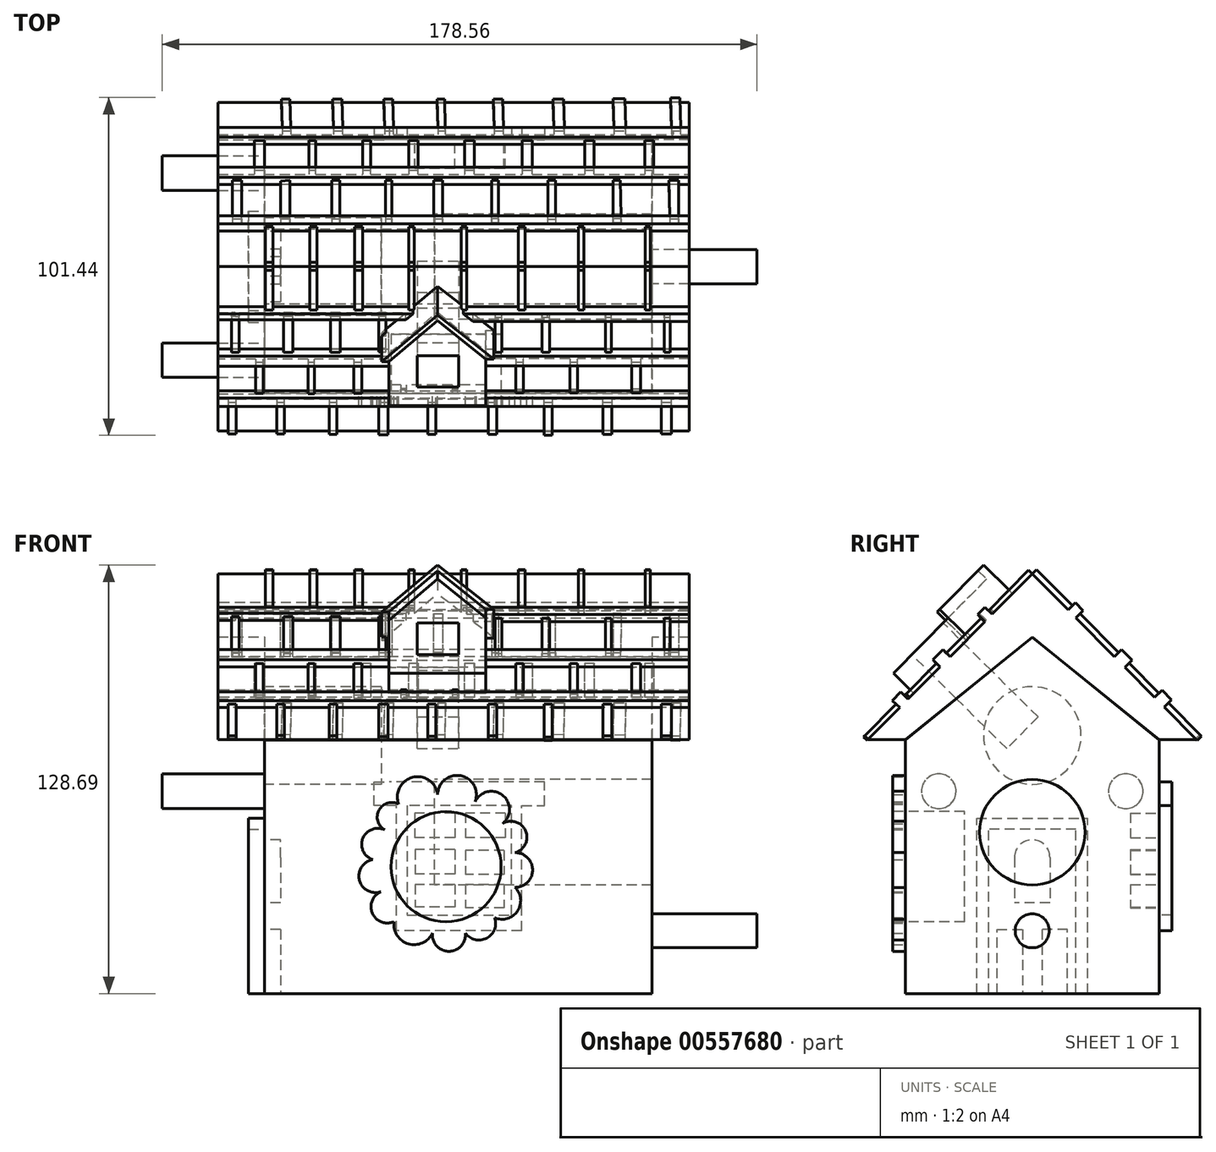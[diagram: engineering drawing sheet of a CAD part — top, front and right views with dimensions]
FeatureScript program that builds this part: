
annotation { "Feature Type Name" : "Feature", "Feature Type Description" : "" }
export const myFeature = defineFeature(function(context is Context, id is Id, definition is map)
    precondition{}
    {
        {
            var Q0;
            Q0=qCreatedBy(makeId("Right.planeOp"),FACE);
            var sketch = newSketch(context, id + "F0", { "sketchPlane" : qUnion([Q0])});
            skLineSegment(sketch, "E0.bottom", {"start": v(38.1, 38.1) * mm, "end": v(-38.1, 38.1) * mm});
            skLineSegment(sketch, "E0.top", {"start": v(38.1, -38.1) * mm, "end": v(-38.1, -38.1) * mm});
            skLineSegment(sketch, "E0.left", {"start": v(38.1, 38.1) * mm, "end": v(38.1, -38.1) * mm});
            skLineSegment(sketch, "E0.right", {"start": v(-38.1, 38.1) * mm, "end": v(-38.1, -38.1) * mm});
            skPoint(sketch, "E0.middle", {"position": v(0, 0) * mm});
            skCircle(sketch, "E1", {"center": v(0, 10.38) * mm, "radius": 15.83 * mm});
            skLineSegment(sketch, "E2", {"start": v(-38.1, 38.1) * mm, "end": v(0, 68.98) * mm});
            skLineSegment(sketch, "E3", {"start": v(0, 68.98) * mm, "end": v(38.1, 38.1) * mm});
            skSolve(sketch);
        }
        {
            var Q0;
            Q0 = qSketchRegion(id + "F0", true);
            extrude(context, id + "F1", {"entities" : qUnion([Q0]), "depth" : 14.73 * mm, "offsetDistance" : 25.4 * mm});
        }
        {
            var Q0;
            Q0=qCreatedBy(makeId("Right.planeOp"),FACE);
            var sketch = newSketch(context, id + "F2", { "sketchPlane" : qUnion([Q0])});
            skCircle(sketch, "E4", {"center": v(0, -19.24) * mm, "radius": 5.12 * mm});
            skSolve(sketch);
        }
        {
            var Q0;
            Q0 = qSketchRegion(id + "F2", true);
            extrude(context, id + "F3", {"entities" : qUnion([Q0]), "operationType" : NewBodyOperationType.ADD, "depth" : 46.23 * mm, "offsetDistance" : 25.4 * mm});
        }
        {
            var Q0;
            Q0=qCreatedBy(makeId("Right.planeOp"),FACE);
            var sketch = newSketch(context, id + "F4", { "sketchPlane" : qUnion([Q0])});
            skLineSegment(sketch, "E5", {"start": v(-38.15, 38.14) * mm, "end": v(0, 68.94) * mm});
            skLineSegment(sketch, "E6.MirrorCS", {"start": v(38.15, 38.14) * mm, "end": v(0, 68.94) * mm});
            skPoint(sketch, "E7.start.orphan", {"position": v(0, 72.65) * mm});
            skPoint(sketch, "E8.start.orphan", {"position": v(-57.02, 39.24) * mm});
            skLineSegment(sketch, "E9", {"start": v(-38.15, 38.14) * mm, "end": v(-44.95, 38.14) * mm});
            skPoint(sketch, "E10.MirrorCS.end.orphan", {"position": v(57.02, 39.24) * mm});
            skPoint(sketch, "E11.MirrorCS.end.orphan", {"position": v(38.15, 38.14) * mm});
            skLineSegment(sketch, "E12.MirrorCS", {"start": v(38.15, 38.14) * mm, "end": v(44.95, 38.14) * mm});
            skLineSegment(sketch, "E13", {"start": v(44.95, 38.14) * mm, "end": v(49.34, 38.14) * mm});
            skLineSegment(sketch, "E14", {"start": v(49.34, 38.14) * mm, "end": v(0, 87.99) * mm});
            skLineSegment(sketch, "E15.MirrorCS", {"start": v(-44.95, 38.14) * mm, "end": v(-49.34, 38.14) * mm});
            skLineSegment(sketch, "E16.MirrorCS", {"start": v(-49.34, 38.14) * mm, "end": v(0, 87.99) * mm});
            skSolve(sketch);
        }
        {
            var Q0;
            Q0 = qSketchRegion(id + "F4", true);
            extrude(context, id + "F5", {"entities" : qUnion([Q0]), "operationType" : NewBodyOperationType.ADD, "depth" : 25.9 * mm, "offsetDistance" : 25.4 * mm});
        }
        {
            var Q0;
            Q0=makeQuery(id+"F5.boolean.opBoolean","MERGE",FACE,{"derivedFrom":[makeQuery(id+"F1.opExtrude","CAP_FACE",FACE,{"disambiguationData":[OSD([sQuery(id+"F0.wireOp",EDGE,"E0.top"),sQuery(id+"F0.wireOp",EDGE,"E0.left"),sQuery(id+"F0.wireOp",EDGE,"E0.right"),sQuery(id+"F0.wireOp",EDGE,"E1"),sQuery(id+"F0.wireOp",EDGE,"E2"),sQuery(id+"F0.wireOp",EDGE,"E3")])],"isStart":true}),makeQuery(id+"F5.opExtrude","CAP_FACE",FACE,{"disambiguationData":[OSD([sQuery(id+"F4.wireOp",EDGE,"E5"),sQuery(id+"F4.wireOp",EDGE,"E6.MirrorCS"),sQuery(id+"F4.wireOp",EDGE,"E9"),sQuery(id+"F4.wireOp",EDGE,"mGPt1msT-ov7u-mBRv-SWqM-muiSPzfu6SFx"),sQuery(id+"F4.wireOp",EDGE,"db452817-d711-4797-9ae9-b6f5df7f732d0.MirrorCS"),sQuery(id+"F4.wireOp",EDGE,"E12.MirrorCS")])],"isStart":true})]});
            extrude(context, id + "F6", {"entities" : qUnion([Q0]), "operationType" : NewBodyOperationType.ADD, "depth" : 101.6 * mm, "offsetDistance" : 25.4 * mm});
        }
        {
            var Q0;
            Q0=makeQuery(id+"F6.opExtrude","CAP_FACE",FACE,{"disambiguationData":[OSD([sQuery(id+"F0.wireOp",EDGE,"E0.top"),sQuery(id+"F0.wireOp",EDGE,"E0.left"),sQuery(id+"F0.wireOp",EDGE,"E0.right"),sQuery(id+"F0.wireOp",EDGE,"E1"),sQuery(id+"F0.wireOp",EDGE,"E2"),sQuery(id+"F0.wireOp",EDGE,"E3"),sQuery(id+"F4.wireOp",EDGE,"E5"),sQuery(id+"F4.wireOp",EDGE,"E6.MirrorCS"),sQuery(id+"F4.wireOp",EDGE,"E9"),sQuery(id+"F4.wireOp",EDGE,"mGPt1msT-ov7u-mBRv-SWqM-muiSPzfu6SFx"),sQuery(id+"F4.wireOp",EDGE,"db452817-d711-4797-9ae9-b6f5df7f732d0.MirrorCS"),sQuery(id+"F4.wireOp",EDGE,"E12.MirrorCS")])],"isStart":false});
            var sketch = newSketch(context, id + "F7", { "sketchPlane" : qUnion([Q0])});
            skCircle(sketch, "E17", {"center": v(0, 10.38) * mm, "radius": 15.83 * mm});
            skPoint(sketch, "E17.first.point", {"position": v(-11.76, 20.98) * mm});
            skPoint(sketch, "E17.second.point", {"position": v(11.95, 0) * mm});
            skPoint(sketch, "E17.third.point", {"position": v(14.73, 16.19) * mm});
            skSolve(sketch);
        }
        {
            var Q0;
            Q0 = qSketchRegion(id + "F7", true);
            extrude(context, id + "F8", {"entities" : qUnion([Q0]), "operationType" : NewBodyOperationType.ADD, "oppositeDirection" : true, "depth" : 51.05 * mm, "offsetDistance" : 25.4 * mm});
        }
        {
            var Q0;
            Q0=makeQuery(id+"F8.boolean.opBoolean","MERGE",FACE,{"derivedFrom":[makeQuery(id+"F6.opExtrude","CAP_FACE",FACE,{"disambiguationData":[OSD([sQuery(id+"F0.wireOp",EDGE,"E0.top"),sQuery(id+"F0.wireOp",EDGE,"E0.left"),sQuery(id+"F0.wireOp",EDGE,"E0.right"),sQuery(id+"F0.wireOp",EDGE,"E1"),sQuery(id+"F0.wireOp",EDGE,"E2"),sQuery(id+"F0.wireOp",EDGE,"E3"),sQuery(id+"F4.wireOp",EDGE,"E5"),sQuery(id+"F4.wireOp",EDGE,"E6.MirrorCS"),sQuery(id+"F4.wireOp",EDGE,"E9"),sQuery(id+"F4.wireOp",EDGE,"mGPt1msT-ov7u-mBRv-SWqM-muiSPzfu6SFx"),sQuery(id+"F4.wireOp",EDGE,"db452817-d711-4797-9ae9-b6f5df7f732d0.MirrorCS"),sQuery(id+"F4.wireOp",EDGE,"E12.MirrorCS")])],"isStart":false}),makeQuery(id+"F8.opExtrude","CAP_FACE",FACE,{"disambiguationData":[OSD([sQuery(id+"F7.wireOp",EDGE,"E17")])],"isStart":true})]});
            var sketch = newSketch(context, id + "F9", { "sketchPlane" : qUnion([Q0])});
            skLineSegment(sketch, "E18", {"start": v(-16.68, -38.1) * mm, "end": v(-16.68, 14.56) * mm});
            skLineSegment(sketch, "E19", {"start": v(-16.68, 14.56) * mm, "end": v(-2.36, 14.56) * mm});
            skLineSegment(sketch, "E20", {"start": v(-13.13, -38.1) * mm, "end": v(-16.68, -38.1) * mm});
            skLineSegment(sketch, "E21.MirrorCS", {"start": v(16.68, 14.56) * mm, "end": v(2.36, 14.56) * mm});
            skLineSegment(sketch, "E22.MirrorCS", {"start": v(16.68, -38.1) * mm, "end": v(16.68, 14.56) * mm});
            skLineSegment(sketch, "E23.MirrorCS", {"start": v(13.13, -38.1) * mm, "end": v(16.68, -38.1) * mm});
            skLineSegment(sketch, "E24", {"start": v(-2.36, 14.56) * mm, "end": v(2.36, 14.56) * mm});
            skLineSegment(sketch, "E25", {"start": v(-13.13, -38.1) * mm, "end": v(-13.13, 11.21) * mm});
            skLineSegment(sketch, "E26", {"start": v(-13.13, 11.21) * mm, "end": v(0, 11.21) * mm});
            skLineSegment(sketch, "E27.MirrorCS", {"start": v(13.13, 11.21) * mm, "end": v(0, 11.21) * mm});
            skLineSegment(sketch, "E28.MirrorCS", {"start": v(13.13, -38.1) * mm, "end": v(13.13, 11.21) * mm});
            skPoint(sketch, "E29.start.orphan", {"position": v(-2.36, -38.1) * mm});
            skPoint(sketch, "E30.orphan", {"position": v(2.36, -38.1) * mm});
            skSolve(sketch);
        }
        {
            var Q0;
            Q0 = qSketchRegion(id + "F9", true);
            extrude(context, id + "F10", {"entities" : qUnion([Q0]), "operationType" : NewBodyOperationType.ADD, "depth" : 4.83 * mm, "offsetDistance" : 25.4 * mm});
        }
        {
            var Q0;
            {var subQ0=sQuery(id+"F0.wireOp",EDGE,"E0.top");Q0=makeQuery(id+"F10.boolean.opBoolean","SPLIT",FACE,{"disambiguationData":[TD([makeQuery(id+"F10.opExtrude","SWEPT_FACE",FACE,{"disambiguationData":[OSD([sQuery(id+"F9.wireOp",EDGE,"E25")])]})])],"derivedFrom":makeQuery(id+"F8.boolean.opBoolean","MERGE",FACE,{"derivedFrom":[makeQuery(id+"F6.opExtrude","CAP_FACE",FACE,{"disambiguationData":[OSD([subQ0,sQuery(id+"F0.wireOp",EDGE,"E0.left"),sQuery(id+"F0.wireOp",EDGE,"E0.right"),sQuery(id+"F0.wireOp",EDGE,"E1"),sQuery(id+"F0.wireOp",EDGE,"E2"),sQuery(id+"F0.wireOp",EDGE,"E3"),sQuery(id+"F4.wireOp",EDGE,"E5"),sQuery(id+"F4.wireOp",EDGE,"E6.MirrorCS"),sQuery(id+"F4.wireOp",EDGE,"E9"),sQuery(id+"F4.wireOp",EDGE,"mGPt1msT-ov7u-mBRv-SWqM-muiSPzfu6SFx"),sQuery(id+"F4.wireOp",EDGE,"db452817-d711-4797-9ae9-b6f5df7f732d0.MirrorCS"),sQuery(id+"F4.wireOp",EDGE,"E12.MirrorCS")])],"isStart":false}),makeQuery(id+"F8.opExtrude","CAP_FACE",FACE,{"disambiguationData":[OSD([sQuery(id+"F7.wireOp",EDGE,"E17")])],"isStart":true})]})});}
            var sketch = newSketch(context, id + "F11", { "sketchPlane" : qUnion([Q0])});
            skLineSegment(sketch, "E31", {"start": v(-5.3, 2.78) * mm, "end": v(-5.3, -10.8) * mm});
            skLineSegment(sketch, "E32.MirrorCS", {"start": v(5.3, 2.78) * mm, "end": v(5.3, -10.8) * mm});
            skArc(sketch, "E33", {"start": v(5.3, 2.78) * mm, "mid": v(0, 8.08) * mm, "end": v(-5.3, 2.78) * mm});
            skLineSegment(sketch, "E34", {"start": v(-5.3, -10.8) * mm, "end": v(5.3, -10.8) * mm});
            skLineSegment(sketch, "E35", {"start": v(-11.37, -12.68) * mm, "end": v(-11.37, -15.43) * mm});
            skLineSegment(sketch, "E36", {"start": v(-11.37, -15.43) * mm, "end": v(10.6, -15.43) * mm});
            skLineSegment(sketch, "E37", {"start": v(10.6, -15.43) * mm, "end": v(10.6, -12.52) * mm});
            skLineSegment(sketch, "E38", {"start": v(10.6, -12.52) * mm, "end": v(-11.37, -12.52) * mm});
            skLineSegment(sketch, "E39", {"start": v(-10.6, -38.1) * mm, "end": v(-10.6, -18.85) * mm});
            skLineSegment(sketch, "E40", {"start": v(-10.6, -18.85) * mm, "end": v(-2.9, -18.85) * mm});
            skLineSegment(sketch, "E41", {"start": v(-2.9, -18.85) * mm, "end": v(-2.9, -38.1) * mm});
            skLineSegment(sketch, "E42", {"start": v(-2.9, -38.1) * mm, "end": v(-10.6, -38.1) * mm});
            skLineSegment(sketch, "E43.MirrorCS", {"start": v(2.9, -18.85) * mm, "end": v(2.9, -38.1) * mm});
            skLineSegment(sketch, "E44.MirrorCS", {"start": v(10.6, -38.1) * mm, "end": v(10.6, -18.85) * mm});
            skLineSegment(sketch, "E45.MirrorCS", {"start": v(10.6, -18.85) * mm, "end": v(2.9, -18.85) * mm});
            skLineSegment(sketch, "E46.MirrorCS", {"start": v(2.9, -38.1) * mm, "end": v(10.6, -38.1) * mm});
            skSolve(sketch);
        }
        {
            var Q0;
            Q0 = qSketchRegion(id + "F11", true);
            extrude(context, id + "F12", {"entities" : qUnion([Q0]), "operationType" : NewBodyOperationType.REMOVE, "oppositeDirection" : true, "depth" : 4.83 * mm, "offsetDistance" : 25.4 * mm});
        }
        {
            var Q0;
            {var subQ0=sQuery(id+"F4.wireOp",EDGE,"E6.MirrorCS");var subQ1=sQuery(id+"F4.wireOp",EDGE,"E5");var subQ2=sQuery(id+"F4.wireOp",EDGE,"E12.MirrorCS");var subQ3=sQuery(id+"F4.wireOp",EDGE,"E9");var subQ4=sQuery(id+"F0.wireOp",EDGE,"E2");var subQ5=sQuery(id+"F4.wireOp",EDGE,"db452817-d711-4797-9ae9-b6f5df7f732d0.MirrorCS");var subQ6=sQuery(id+"F0.wireOp",EDGE,"E0.right");var subQ7=sQuery(id+"F4.wireOp",EDGE,"mGPt1msT-ov7u-mBRv-SWqM-muiSPzfu6SFx");var subQ8=sQuery(id+"F0.wireOp",EDGE,"E0.left");var subQ9=sQuery(id+"F0.wireOp",EDGE,"E3");var subQ10=sQuery(id+"F0.wireOp",EDGE,"E0.top");Q0=makeQuery(id+"F10.boolean.opBoolean","SPLIT",FACE,{"disambiguationData":[TD([makeQuery(id+"F1.opExtrude","SWEPT_FACE",FACE,{"disambiguationData":[OSD([subQ8])]})])],"derivedFrom":makeQuery(id+"F8.boolean.opBoolean","MERGE",FACE,{"derivedFrom":[makeQuery(id+"F6.opExtrude","CAP_FACE",FACE,{"disambiguationData":[OSD([subQ10,subQ8,subQ6,sQuery(id+"F0.wireOp",EDGE,"E1"),subQ4,subQ9,subQ1,subQ0,subQ3,subQ7,subQ5,subQ2])],"isStart":false}),makeQuery(id+"F8.opExtrude","CAP_FACE",FACE,{"disambiguationData":[OSD([sQuery(id+"F7.wireOp",EDGE,"E17")])],"isStart":true})]})});}
            var sketch = newSketch(context, id + "F13", { "sketchPlane" : qUnion([Q0])});
            skCircle(sketch, "E47", {"center": v(0, 39.42) * mm, "radius": 14.66 * mm});
            skSolve(sketch);
        }
        {
            var Q0;
            Q0 = qSketchRegion(id + "F13", true);
            extrude(context, id + "F14", {"entities" : qUnion([Q0]), "operationType" : NewBodyOperationType.REMOVE, "oppositeDirection" : true, "depth" : 35.05 * mm, "offsetDistance" : 25.4 * mm});
        }
        {
            var Q0;
            {var subQ0=sQuery(id+"F4.wireOp",EDGE,"E6.MirrorCS");var subQ1=sQuery(id+"F4.wireOp",EDGE,"E5");var subQ2=sQuery(id+"F4.wireOp",EDGE,"E12.MirrorCS");var subQ3=sQuery(id+"F4.wireOp",EDGE,"E9");var subQ4=sQuery(id+"F0.wireOp",EDGE,"E2");var subQ5=sQuery(id+"F4.wireOp",EDGE,"db452817-d711-4797-9ae9-b6f5df7f732d0.MirrorCS");var subQ6=sQuery(id+"F0.wireOp",EDGE,"E0.right");var subQ7=sQuery(id+"F4.wireOp",EDGE,"mGPt1msT-ov7u-mBRv-SWqM-muiSPzfu6SFx");var subQ8=sQuery(id+"F0.wireOp",EDGE,"E0.left");var subQ9=sQuery(id+"F0.wireOp",EDGE,"E3");var subQ10=sQuery(id+"F0.wireOp",EDGE,"E0.top");Q0=makeQuery(id+"F10.boolean.opBoolean","SPLIT",FACE,{"disambiguationData":[TD([makeQuery(id+"F1.opExtrude","SWEPT_FACE",FACE,{"disambiguationData":[OSD([subQ8])]})])],"derivedFrom":makeQuery(id+"F8.boolean.opBoolean","MERGE",FACE,{"derivedFrom":[makeQuery(id+"F6.opExtrude","CAP_FACE",FACE,{"disambiguationData":[OSD([subQ10,subQ8,subQ6,sQuery(id+"F0.wireOp",EDGE,"E1"),subQ4,subQ9,subQ1,subQ0,subQ3,subQ7,subQ5,subQ2])],"isStart":false}),makeQuery(id+"F8.opExtrude","CAP_FACE",FACE,{"disambiguationData":[OSD([sQuery(id+"F7.wireOp",EDGE,"E17")])],"isStart":true})]})});}
            var sketch = newSketch(context, id + "F15", { "sketchPlane" : qUnion([Q0])});
            skCircle(sketch, "E48", {"center": v(-28.08, 22.67) * mm, "radius": 5.2 * mm});
            skCircle(sketch, "E49.MirrorC", {"center": v(28.08, 22.67) * mm, "radius": 5.2 * mm});
            skSolve(sketch);
        }
        {
            var Q0;
            Q0 = qSketchRegion(id + "F15", true);
            extrude(context, id + "F16", {"entities" : qUnion([Q0]), "operationType" : NewBodyOperationType.ADD, "depth" : 30.73 * mm, "offsetDistance" : 25.4 * mm});
        }
        {
            var Q0;
            {var subQ0=sQuery(id+"F4.wireOp",EDGE,"E6.MirrorCS");var subQ1=sQuery(id+"F4.wireOp",EDGE,"E5");var subQ2=sQuery(id+"F4.wireOp",EDGE,"E16.MirrorCS");var subQ3=sQuery(id+"F4.wireOp",EDGE,"E15.MirrorCS");var subQ4=sQuery(id+"F4.wireOp",EDGE,"E9");var subQ5=sQuery(id+"F0.wireOp",EDGE,"E2");var subQ6=sQuery(id+"F4.wireOp",EDGE,"E14");var subQ7=sQuery(id+"F0.wireOp",EDGE,"E0.right");var subQ8=sQuery(id+"F4.wireOp",EDGE,"E13");var subQ9=sQuery(id+"F4.wireOp",EDGE,"E12.MirrorCS");var subQ10=sQuery(id+"F0.wireOp",EDGE,"E0.left");var subQ11=sQuery(id+"F0.wireOp",EDGE,"E3");var subQ12=sQuery(id+"F0.wireOp",EDGE,"E0.top");Q0=makeQuery(id+"F10.boolean.opBoolean","SPLIT",FACE,{"disambiguationData":[TD([makeQuery(id+"F1.opExtrude","SWEPT_FACE",FACE,{"disambiguationData":[OSD([subQ10])]})])],"derivedFrom":makeQuery(id+"F8.boolean.opBoolean","MERGE",FACE,{"derivedFrom":[makeQuery(id+"F6.opExtrude","CAP_FACE",FACE,{"disambiguationData":[OSD([subQ12,subQ10,subQ7,sQuery(id+"F0.wireOp",EDGE,"E1"),subQ5,subQ11,subQ1,subQ0,subQ4,subQ9,subQ8,subQ6,subQ3,subQ2])],"isStart":false}),makeQuery(id+"F8.opExtrude","CAP_FACE",FACE,{"disambiguationData":[OSD([sQuery(id+"F7.wireOp",EDGE,"E17")])],"isStart":true})]})});}
            var sketch = newSketch(context, id + "F17", { "sketchPlane" : qUnion([Q0])});
            skLineSegment(sketch, "E50", {"start": v(-49.34, 38.14) * mm, "end": v(0, 87.99) * mm});
            skLineSegment(sketch, "E51", {"start": v(0, 87.99) * mm, "end": v(49.34, 38.14) * mm});
            skLineSegment(sketch, "E52", {"start": v(49.34, 38.14) * mm, "end": v(38.15, 38.14) * mm});
            skLineSegment(sketch, "E53", {"start": v(-49.34, 38.14) * mm, "end": v(-38.15, 38.14) * mm});
            skLineSegment(sketch, "E54", {"start": v(-38.15, 38.14) * mm, "end": v(0, 69.05) * mm});
            skLineSegment(sketch, "E55", {"start": v(0, 69.05) * mm, "end": v(38.15, 38.14) * mm});
            skSolve(sketch);
        }
        {
            var Q0;
            Q0 = qSketchRegion(id + "F17", true);
            extrude(context, id + "F18", {"entities" : qUnion([Q0]), "operationType" : NewBodyOperationType.ADD, "depth" : 13.97 * mm, "offsetDistance" : 25.4 * mm});
        }
        {
            var Q0;
            {var subQ0=sQuery(id+"F4.wireOp",EDGE,"E16.MirrorCS");Q0=makeQuery(id+"F18.boolean.opBoolean","MERGE",FACE,{"derivedFrom":[makeQuery(id+"F6.boolean.opBoolean","MERGE",FACE,{"derivedFrom":[makeQuery(id+"F5.opExtrude","SWEPT_FACE",FACE,{"disambiguationData":[OSD([subQ0])]}),makeQuery(id+"F6.opExtrude","SWEPT_FACE",FACE,{"disambiguationData":[OSD([subQ0])]})]}),makeQuery(id+"F18.opExtrude","SWEPT_FACE",FACE,{"disambiguationData":[OSD([sQuery(id+"F17.wireOp",EDGE,"E51")])]})]});}
            var sketch = newSketch(context, id + "F19", { "sketchPlane" : qUnion([Q0])});
            skLineSegment(sketch, "E56", {"start": v(-64.2, 11.96) * mm, "end": v(-64.2, 34.31) * mm});
            skLineSegment(sketch, "E57", {"start": v(-64.2, 34.31) * mm, "end": v(-49.73, 51.77) * mm});
            skLineSegment(sketch, "E58", {"start": v(-49.73, 51.77) * mm, "end": v(-35.25, 35.38) * mm});
            skLineSegment(sketch, "E59", {"start": v(-35.25, 35.38) * mm, "end": v(-35.25, 11.96) * mm});
            skLineSegment(sketch, "E60", {"start": v(-35.25, 11.96) * mm, "end": v(-64.2, 11.96) * mm});
            skSolve(sketch);
        }
        {
            var Q0;
            Q0=makeQuery(id+"F19.imprint","IMPRINT",FACE,{"disambiguationData":[TD([[makeQuery(id+"F19.imprint","IMPRINT",EDGE,{"derivedFrom":sQuery(id+"F19.wireOp",EDGE,"E56")}),-1.0]])]});
            extrude(context, id + "F20", {"entities" : qUnion([Q0]), "operationType" : NewBodyOperationType.ADD, "depth" : 8.64 * mm, "offsetDistance" : 25.4 * mm});
        }
        {
            var Q0;
            {var subQ0=sQuery(id+"F4.wireOp",EDGE,"E16.MirrorCS");Q0=makeQuery(id+"F18.boolean.opBoolean","MERGE",FACE,{"derivedFrom":[makeQuery(id+"F6.boolean.opBoolean","MERGE",FACE,{"derivedFrom":[makeQuery(id+"F5.opExtrude","SWEPT_FACE",FACE,{"disambiguationData":[OSD([subQ0])]}),makeQuery(id+"F6.opExtrude","SWEPT_FACE",FACE,{"disambiguationData":[OSD([subQ0])]})]}),makeQuery(id+"F18.opExtrude","SWEPT_FACE",FACE,{"disambiguationData":[OSD([sQuery(id+"F17.wireOp",EDGE,"E51")])]})]});}
            var sketch = newSketch(context, id + "F21", { "sketchPlane" : qUnion([Q0])});
            skLineSegment(sketch, "E61", {"start": v(-35.25, 35.38) * mm, "end": v(-32.72, 35.38) * mm});
            skLineSegment(sketch, "E62", {"start": v(-32.72, 35.38) * mm, "end": v(-49.73, 54.13) * mm});
            skLineSegment(sketch, "E63", {"start": v(-64.2, 34.31) * mm, "end": v(-66.44, 34.31) * mm});
            skLineSegment(sketch, "E64", {"start": v(-66.44, 34.31) * mm, "end": v(-49.73, 54.13) * mm});
            skLineSegment(sketch, "E65", {"start": v(-64.2, 34.31) * mm, "end": v(-49.73, 51.77) * mm});
            skLineSegment(sketch, "E66", {"start": v(-49.73, 51.77) * mm, "end": v(-35.25, 35.38) * mm});
            skSolve(sketch);
        }
        {
            var Q0;
            Q0 = qSketchRegion(id + "F21", true);
            extrude(context, id + "F22", {"entities" : qUnion([Q0]), "operationType" : NewBodyOperationType.ADD, "depth" : 12.2 * mm, "offsetDistance" : 25.4 * mm});
        }
        {
            var Q0;
            Q0=makeQuery(id+"F20.opExtrude","CAP_FACE",FACE,{"disambiguationData":[OSD([sQuery(id+"F19.wireOp",EDGE,"E56"),sQuery(id+"F19.wireOp",EDGE,"E57"),sQuery(id+"F19.wireOp",EDGE,"E58"),sQuery(id+"F19.wireOp",EDGE,"E59"),sQuery(id+"F19.wireOp",EDGE,"E60")])],"isStart":false});
            var sketch = newSketch(context, id + "F23", { "sketchPlane" : qUnion([Q0])});
            skLineSegment(sketch, "E67.bottom", {"start": v(-55.74, 33.2) * mm, "end": v(-43.38, 33.2) * mm});
            skLineSegment(sketch, "E67.top", {"start": v(-55.74, 19.83) * mm, "end": v(-43.38, 19.83) * mm});
            skLineSegment(sketch, "E67.left", {"start": v(-55.74, 33.2) * mm, "end": v(-55.74, 19.83) * mm});
            skLineSegment(sketch, "E67.right", {"start": v(-43.38, 33.2) * mm, "end": v(-43.38, 19.83) * mm});
            skSolve(sketch);
        }
        {
            var Q0;
            Q0 = qSketchRegion(id + "F23", true);
            extrude(context, id + "F24", {"entities" : qUnion([Q0]), "operationType" : NewBodyOperationType.REMOVE, "oppositeDirection" : true, "depth" : 40.13 * mm, "offsetDistance" : 25.4 * mm});
        }
        {
            var Q0;
            {var subQ0=sQuery(id+"F0.wireOp",EDGE,"E0.right");Q0=makeQuery(id+"F6.boolean.opBoolean","MERGE",FACE,{"derivedFrom":[makeQuery(id+"F1.opExtrude","SWEPT_FACE",FACE,{"disambiguationData":[OSD([subQ0])]}),makeQuery(id+"F6.opExtrude","SWEPT_FACE",FACE,{"disambiguationData":[OSD([subQ0])]})]});}
            var sketch = newSketch(context, id + "F25", { "sketchPlane" : qUnion([Q0])});
            skArc(sketch, "E68", {"start": v(-49.62, 21.7) * mm, "mid": v(-57.13, 26.86) * mm, "end": v(-61.3, 18.76) * mm});
            skArc(sketch, "E69", {"start": v(-38.55, 19.18) * mm, "mid": v(-42.53, 27.3) * mm, "end": v(-49.62, 21.7) * mm});
            skArc(sketch, "E70", {"start": v(-30.16, 12.93) * mm, "mid": v(-30.25, 21.56) * mm, "end": v(-38.55, 19.18) * mm});
            skArc(sketch, "E71", {"start": v(-26.4, 4.22) * mm, "mid": v(-23.22, 10.76) * mm, "end": v(-30.16, 12.93) * mm});
            skArc(sketch, "E72", {"start": v(-26.4, -6.21) * mm, "mid": v(-21.13, -1) * mm, "end": v(-26.4, 4.22) * mm});
            skArc(sketch, "E73", {"start": v(-32.5, -15.3) * mm, "mid": v(-25.65, -13.32) * mm, "end": v(-26.4, -6.21) * mm});
            skArc(sketch, "E74", {"start": v(-41.34, -19.93) * mm, "mid": v(-34.92, -21.46) * mm, "end": v(-32.5, -15.3) * mm});
            skArc(sketch, "E75", {"start": v(-51.17, -19.93) * mm, "mid": v(-46.26, -25.43) * mm, "end": v(-41.34, -19.93) * mm});
            skArc(sketch, "E76", {"start": v(-62.73, -16.5) * mm, "mid": v(-58.42, -23.17) * mm, "end": v(-51.17, -19.93) * mm});
            skArc(sketch, "E77", {"start": v(-66.63, -7.5) * mm, "mid": v(-69.24, -13.98) * mm, "end": v(-62.73, -16.5) * mm});
            skArc(sketch, "E78", {"start": v(-69.09, 2.12) * mm, "mid": v(-73.1, -4.03) * mm, "end": v(-66.63, -7.5) * mm});
            skArc(sketch, "E79", {"start": v(-65.2, 10.88) * mm, "mid": v(-72.02, 8.67) * mm, "end": v(-69.09, 2.12) * mm});
            skArc(sketch, "E80", {"start": v(-61.3, 18.76) * mm, "mid": v(-67.32, 16.84) * mm, "end": v(-65.2, 10.88) * mm});
            skSolve(sketch);
        }
        {
            var Q0;
            Q0 = qSketchRegion(id + "F25", true);
            extrude(context, id + "F26", {"entities" : qUnion([Q0]), "operationType" : NewBodyOperationType.ADD, "depth" : 3.8 * mm, "offsetDistance" : 25.4 * mm});
        }
        {
            var Q0;
            Q0=makeQuery(id+"F26.opExtrude","CAP_FACE",FACE,{"disambiguationData":[OSD([sQuery(id+"F25.wireOp",EDGE,"E68"),sQuery(id+"F25.wireOp",EDGE,"E69"),sQuery(id+"F25.wireOp",EDGE,"E70"),sQuery(id+"F25.wireOp",EDGE,"E71"),sQuery(id+"F25.wireOp",EDGE,"E72"),sQuery(id+"F25.wireOp",EDGE,"E73"),sQuery(id+"F25.wireOp",EDGE,"E74"),sQuery(id+"F25.wireOp",EDGE,"E75"),sQuery(id+"F25.wireOp",EDGE,"E76"),sQuery(id+"F25.wireOp",EDGE,"E77"),sQuery(id+"F25.wireOp",EDGE,"E78"),sQuery(id+"F25.wireOp",EDGE,"E79"),sQuery(id+"F25.wireOp",EDGE,"E80")])],"isStart":false});
            var sketch = newSketch(context, id + "F27", { "sketchPlane" : qUnion([Q0])});
            skCircle(sketch, "E81", {"center": v(-47.11, 0) * mm, "radius": 16.53 * mm});
            skSolve(sketch);
        }
        {
            var Q0;
            Q0 = qSketchRegion(id + "F27", true);
            extrude(context, id + "F28", {"entities" : qUnion([Q0]), "operationType" : NewBodyOperationType.REMOVE, "oppositeDirection" : true, "depth" : 21.59 * mm, "offsetDistance" : 25.4 * mm});
        }
        {
            var Q0;
            {var subQ0=sQuery(id+"F0.wireOp",EDGE,"E0.left");Q0=makeQuery(id+"F6.boolean.opBoolean","MERGE",FACE,{"derivedFrom":[makeQuery(id+"F1.opExtrude","SWEPT_FACE",FACE,{"disambiguationData":[OSD([subQ0])]}),makeQuery(id+"F6.opExtrude","SWEPT_FACE",FACE,{"disambiguationData":[OSD([subQ0])]})]});}
            var sketch = newSketch(context, id + "F29", { "sketchPlane" : qUnion([Q0])});
            skLineSegment(sketch, "E82", {"start": v(24.4, -19.25) * mm, "end": v(24.4, 18.4) * mm});
            skLineSegment(sketch, "E83", {"start": v(24.4, 18.4) * mm, "end": v(17.55, 18.4) * mm});
            skLineSegment(sketch, "E84", {"start": v(17.55, 18.4) * mm, "end": v(17.55, 25.45) * mm});
            skLineSegment(sketch, "E85", {"start": v(17.55, 25.45) * mm, "end": v(64.18, 25.45) * mm});
            skLineSegment(sketch, "E86", {"start": v(24.4, -19.25) * mm, "end": v(62.04, -19.25) * mm});
            skLineSegment(sketch, "E87", {"start": v(62.04, -19.25) * mm, "end": v(62.04, 16.9) * mm});
            skPoint(sketch, "E88.startSnap0", {"position": v(20.98, 18.4) * mm});
            skLineSegment(sketch, "E89", {"start": v(58.85, 18.4) * mm, "end": v(58.85, -14.51) * mm});
            skLineSegment(sketch, "E90", {"start": v(58.85, -14.51) * mm, "end": v(27.43, -14.51) * mm});
            skPoint(sketch, "E88.start.orphan", {"position": v(26.74, 18.4) * mm});
            skPoint(sketch, "E91.end.orphan", {"position": v(67.82, 25.24) * mm});
            skPoint(sketch, "E92.end.orphan", {"position": v(67.82, 25.45) * mm});
            skLineSegment(sketch, "E93", {"start": v(27.43, -14.51) * mm, "end": v(27.43, 16.38) * mm});
            skLineSegment(sketch, "E94", {"start": v(27.43, 16.38) * mm, "end": v(27.43, 18.4) * mm});
            skLineSegment(sketch, "E95", {"start": v(27.43, 18.4) * mm, "end": v(58.85, 18.4) * mm});
            skLineSegment(sketch, "E96", {"start": v(62.04, 16.9) * mm, "end": v(62.04, 18.4) * mm});
            skLineSegment(sketch, "E97", {"start": v(62.04, 18.4) * mm, "end": v(68.65, 18.4) * mm});
            skLineSegment(sketch, "E98", {"start": v(68.65, 18.4) * mm, "end": v(68.65, 25.5) * mm});
            skLineSegment(sketch, "E99", {"start": v(68.65, 25.5) * mm, "end": v(64.18, 25.45) * mm});
            skSolve(sketch);
        }
        {
            var Q0;
            Q0=makeQuery(id+"F29.imprint","IMPRINT",FACE,{"disambiguationData":[TD([[makeQuery(id+"F29.imprint","IMPRINT",EDGE,{"derivedFrom":sQuery(id+"F29.wireOp",EDGE,"E82")}),-1.0]])]});
            extrude(context, id + "F30", {"entities" : qUnion([Q0]), "operationType" : NewBodyOperationType.ADD, "depth" : 3.8 * mm, "offsetDistance" : 25.4 * mm});
        }
        {
            var Q0;
            {var subQ0=sQuery(id+"F0.wireOp",EDGE,"E0.left");Q0=makeQuery(id+"F30.boolean.opBoolean","SPLIT",FACE,{"disambiguationData":[TD([makeQuery(id+"F30.opExtrude","SWEPT_FACE",FACE,{"disambiguationData":[OSD([sQuery(id+"F29.wireOp",EDGE,"E89")])]})])],"derivedFrom":makeQuery(id+"F6.boolean.opBoolean","MERGE",FACE,{"derivedFrom":[makeQuery(id+"F1.opExtrude","SWEPT_FACE",FACE,{"disambiguationData":[OSD([subQ0])]}),makeQuery(id+"F6.opExtrude","SWEPT_FACE",FACE,{"disambiguationData":[OSD([subQ0])]})]})});}
            var sketch = newSketch(context, id + "F31", { "sketchPlane" : qUnion([Q0])});
            skLineSegment(sketch, "E100.bottom", {"start": v(29.3, 16.13) * mm, "end": v(41.25, 16.13) * mm});
            skLineSegment(sketch, "E100.top", {"start": v(29.3, 8.75) * mm, "end": v(41.25, 8.75) * mm});
            skLineSegment(sketch, "E100.left", {"start": v(29.3, 16.13) * mm, "end": v(29.3, 8.75) * mm});
            skLineSegment(sketch, "E100.right", {"start": v(41.25, 16.13) * mm, "end": v(41.25, 8.75) * mm});
            skLineSegment(sketch, "E101.bottom", {"start": v(29.7, 4.86) * mm, "end": v(41.25, 4.86) * mm});
            skLineSegment(sketch, "E101.top", {"start": v(29.7, -2.38) * mm, "end": v(41.25, -2.38) * mm});
            skLineSegment(sketch, "E101.left", {"start": v(29.7, 4.86) * mm, "end": v(29.7, -2.38) * mm});
            skLineSegment(sketch, "E101.right", {"start": v(41.25, 4.86) * mm, "end": v(41.25, -2.38) * mm});
            skLineSegment(sketch, "E102.bottom", {"start": v(29.7, -5.33) * mm, "end": v(41.25, -5.33) * mm});
            skLineSegment(sketch, "E102.top", {"start": v(29.7, -12.3) * mm, "end": v(41.25, -12.3) * mm});
            skLineSegment(sketch, "E102.left", {"start": v(29.7, -5.33) * mm, "end": v(29.7, -12.3) * mm});
            skLineSegment(sketch, "E102.right", {"start": v(41.25, -5.33) * mm, "end": v(41.25, -12.3) * mm});
            skLineSegment(sketch, "E103.bottom", {"start": v(44.47, 16.13) * mm, "end": v(56.54, 16.13) * mm});
            skLineSegment(sketch, "E103.top", {"start": v(44.47, 8.75) * mm, "end": v(56.54, 8.75) * mm});
            skLineSegment(sketch, "E103.left", {"start": v(44.47, 16.13) * mm, "end": v(44.47, 8.75) * mm});
            skLineSegment(sketch, "E103.right", {"start": v(56.54, 16.13) * mm, "end": v(56.54, 8.75) * mm});
            skLineSegment(sketch, "E104.bottom", {"start": v(44.47, 5.13) * mm, "end": v(56.4, 5.13) * mm});
            skLineSegment(sketch, "E104.top", {"start": v(44.47, -2.25) * mm, "end": v(56.4, -2.25) * mm});
            skLineSegment(sketch, "E104.left", {"start": v(44.47, 5.13) * mm, "end": v(44.47, -2.25) * mm});
            skLineSegment(sketch, "E104.right", {"start": v(56.4, 5.13) * mm, "end": v(56.4, -2.25) * mm});
            skLineSegment(sketch, "E105.bottom", {"start": v(44.47, -5.33) * mm, "end": v(56.4, -5.33) * mm});
            skLineSegment(sketch, "E105.top", {"start": v(44.47, -12.17) * mm, "end": v(56.4, -12.17) * mm});
            skLineSegment(sketch, "E105.left", {"start": v(44.47, -5.33) * mm, "end": v(44.47, -12.17) * mm});
            skLineSegment(sketch, "E105.right", {"start": v(56.4, -5.33) * mm, "end": v(56.4, -12.17) * mm});
            skSolve(sketch);
        }
        {
            var Q0;
            Q0 = qSketchRegion(id + "F31", true);
            extrude(context, id + "F32", {"entities" : qUnion([Q0]), "operationType" : NewBodyOperationType.REMOVE, "oppositeDirection" : true, "depth" : 8.64 * mm, "offsetDistance" : 25.4 * mm});
        }
        {
            var Q0;
            {var subQ0=sQuery(id+"F4.wireOp",EDGE,"E14");Q0=makeQuery(id+"F18.boolean.opBoolean","MERGE",FACE,{"derivedFrom":[makeQuery(id+"F6.boolean.opBoolean","MERGE",FACE,{"derivedFrom":[makeQuery(id+"F5.opExtrude","SWEPT_FACE",FACE,{"disambiguationData":[OSD([subQ0])]}),makeQuery(id+"F6.opExtrude","SWEPT_FACE",FACE,{"disambiguationData":[OSD([subQ0])]})]}),makeQuery(id+"F18.opExtrude","SWEPT_FACE",FACE,{"disambiguationData":[OSD([sQuery(id+"F17.wireOp",EDGE,"E50")])]})]});}
            var sketch = newSketch(context, id + "F33", { "sketchPlane" : qUnion([Q0])});
            skLineSegment(sketch, "E106", {"start": v(-25.9, 47.26) * mm, "end": v(115.57, 47.26) * mm});
            skLineSegment(sketch, "E107", {"start": v(115.57, 47.26) * mm, "end": v(115.57, 43.97) * mm});
            skLineSegment(sketch, "E108", {"start": v(115.57, 43.97) * mm, "end": v(-25.9, 43.97) * mm});
            skLineSegment(sketch, "E109", {"start": v(-25.9, 43.97) * mm, "end": v(-25.9, 47.26) * mm});
            skLineSegment(sketch, "E110", {"start": v(-25.9, 27.47) * mm, "end": v(115.57, 27.47) * mm});
            skLineSegment(sketch, "E111", {"start": v(115.57, 27.47) * mm, "end": v(115.57, 23.05) * mm});
            skLineSegment(sketch, "E112", {"start": v(115.57, 23.05) * mm, "end": v(-25.9, 23.05) * mm});
            skLineSegment(sketch, "E113", {"start": v(-25.9, 23.05) * mm, "end": v(-25.9, 27.47) * mm});
            skLineSegment(sketch, "E114", {"start": v(-25.9, 10.27) * mm, "end": v(115.57, 10.27) * mm});
            skLineSegment(sketch, "E115", {"start": v(115.57, 10.27) * mm, "end": v(115.57, 6.24) * mm});
            skLineSegment(sketch, "E116", {"start": v(115.57, 6.24) * mm, "end": v(-25.9, 6.24) * mm});
            skLineSegment(sketch, "E117", {"start": v(-25.9, 6.24) * mm, "end": v(-25.9, 10.27) * mm});
            skSolve(sketch);
        }
        {
            var Q0;
            Q0 = qSketchRegion(id + "F33", true);
            extrude(context, id + "F34", {"entities" : qUnion([Q0]), "operationType" : NewBodyOperationType.ADD, "depth" : 3.05 * mm, "offsetDistance" : 25.4 * mm});
        }
        {
            var Q0;
            {var subQ0=sQuery(id+"F4.wireOp",EDGE,"E16.MirrorCS");var subQ1=sQuery(id+"F4.wireOp",EDGE,"E14");var subQ3=sQuery(id+"F17.wireOp",EDGE,"E50");Q0=makeQuery(id+"F34.boolean.opBoolean","SPLIT",FACE,{"disambiguationData":[TD([makeQuery(id+"F5.opExtrude","SWEPT_FACE",FACE,{"disambiguationData":[OSD([subQ0])]})])],"derivedFrom":makeQuery(id+"F18.boolean.opBoolean","MERGE",FACE,{"derivedFrom":[makeQuery(id+"F6.boolean.opBoolean","MERGE",FACE,{"derivedFrom":[makeQuery(id+"F5.opExtrude","SWEPT_FACE",FACE,{"disambiguationData":[OSD([subQ1])]}),makeQuery(id+"F6.opExtrude","SWEPT_FACE",FACE,{"disambiguationData":[OSD([subQ1])]})]}),makeQuery(id+"F18.opExtrude","SWEPT_FACE",FACE,{"disambiguationData":[OSD([subQ3])]})]})});}
            var sketch = newSketch(context, id + "F35", { "sketchPlane" : qUnion([Q0])});
            skLineSegment(sketch, "E118", {"start": v(-14.2, 47.26) * mm, "end": v(-14.2, 62.54) * mm});
            skLineSegment(sketch, "E119", {"start": v(-14.2, 62.54) * mm, "end": v(-12.63, 62.54) * mm});
            skLineSegment(sketch, "E120", {"start": v(-12.63, 62.54) * mm, "end": v(-12.63, 47.26) * mm});
            skLineSegment(sketch, "E121", {"start": v(-12.63, 47.26) * mm, "end": v(-14.2, 47.26) * mm});
            skLineSegment(sketch, "E122", {"start": v(5.79, 47.26) * mm, "end": v(5.79, 62.54) * mm});
            skLineSegment(sketch, "E123", {"start": v(5.79, 62.54) * mm, "end": v(7.35, 62.54) * mm});
            skLineSegment(sketch, "E124", {"start": v(7.35, 62.54) * mm, "end": v(7.35, 47.26) * mm});
            skLineSegment(sketch, "E125", {"start": v(7.35, 47.26) * mm, "end": v(5.79, 47.26) * mm});
            skLineSegment(sketch, "E126", {"start": v(23.42, 47.26) * mm, "end": v(23.42, 62.54) * mm});
            skLineSegment(sketch, "E127", {"start": v(23.42, 62.54) * mm, "end": v(25.37, 62.54) * mm});
            skLineSegment(sketch, "E128", {"start": v(25.37, 62.54) * mm, "end": v(25.37, 47.26) * mm});
            skLineSegment(sketch, "E129", {"start": v(25.37, 47.26) * mm, "end": v(23.42, 47.26) * mm});
            skLineSegment(sketch, "E130", {"start": v(40.84, 62.54) * mm, "end": v(40.84, 47.26) * mm});
            skLineSegment(sketch, "E131", {"start": v(40.84, 47.26) * mm, "end": v(42.62, 47.26) * mm});
            skLineSegment(sketch, "E132", {"start": v(42.62, 47.26) * mm, "end": v(42.62, 62.54) * mm});
            skLineSegment(sketch, "E133", {"start": v(42.62, 62.54) * mm, "end": v(40.84, 62.54) * mm});
            skLineSegment(sketch, "E134", {"start": v(56.7, 62.54) * mm, "end": v(56.7, 47.26) * mm});
            skLineSegment(sketch, "E135", {"start": v(56.7, 47.26) * mm, "end": v(58.27, 47.26) * mm});
            skLineSegment(sketch, "E136", {"start": v(58.27, 47.26) * mm, "end": v(58.27, 62.54) * mm});
            skLineSegment(sketch, "E137", {"start": v(58.27, 62.54) * mm, "end": v(56.7, 62.54) * mm});
            skLineSegment(sketch, "E138", {"start": v(72.18, 62.54) * mm, "end": v(72.18, 47.26) * mm});
            skLineSegment(sketch, "E139", {"start": v(72.18, 47.26) * mm, "end": v(74.54, 47.26) * mm});
            skLineSegment(sketch, "E140", {"start": v(74.54, 47.26) * mm, "end": v(74.54, 62.54) * mm});
            skLineSegment(sketch, "E141", {"start": v(74.54, 62.54) * mm, "end": v(72.18, 62.54) * mm});
            skLineSegment(sketch, "E142", {"start": v(85.9, 62.54) * mm, "end": v(85.9, 47.26) * mm});
            skLineSegment(sketch, "E143", {"start": v(85.9, 47.26) * mm, "end": v(88, 47.26) * mm});
            skLineSegment(sketch, "E144", {"start": v(88, 47.26) * mm, "end": v(88, 62.54) * mm});
            skLineSegment(sketch, "E145", {"start": v(88, 62.54) * mm, "end": v(85.9, 62.54) * mm});
            skLineSegment(sketch, "E146", {"start": v(99.13, 62.54) * mm, "end": v(99.13, 47.26) * mm});
            skLineSegment(sketch, "E147", {"start": v(99.13, 47.26) * mm, "end": v(101.36, 47.26) * mm});
            skLineSegment(sketch, "E148", {"start": v(101.36, 47.26) * mm, "end": v(101.36, 62.54) * mm});
            skLineSegment(sketch, "E149", {"start": v(101.36, 62.54) * mm, "end": v(99.13, 62.54) * mm});
            skLineSegment(sketch, "E150", {"start": v(-5.49, 43.95) * mm, "end": v(-3.03, 43.95) * mm});
            skLineSegment(sketch, "E151", {"start": v(-3.03, 43.95) * mm, "end": v(-3.03, 27.48) * mm});
            skLineSegment(sketch, "E152", {"start": v(-3.03, 27.48) * mm, "end": v(-5.25, 27.48) * mm});
            skLineSegment(sketch, "E153", {"start": v(-5.25, 27.48) * mm, "end": v(-3.03, 27.48) * mm});
            skLineSegment(sketch, "E154", {"start": v(14.27, 27.48) * mm, "end": v(14.27, 44) * mm});
            skLineSegment(sketch, "E155", {"start": v(14.27, 44) * mm, "end": v(16.5, 44) * mm});
            skLineSegment(sketch, "E156", {"start": v(16.5, 44) * mm, "end": v(16.5, 27.48) * mm});
            skLineSegment(sketch, "E157", {"start": v(16.5, 27.48) * mm, "end": v(14.27, 27.48) * mm});
            skLineSegment(sketch, "E158", {"start": v(31.4, 43.9) * mm, "end": v(31.4, 27.48) * mm});
            skLineSegment(sketch, "E159", {"start": v(-5.49, 43.95) * mm, "end": v(-5.25, 27.48) * mm});
            skLineSegment(sketch, "E160", {"start": v(31.4, 43.9) * mm, "end": v(33.4, 43.9) * mm});
            skLineSegment(sketch, "E161", {"start": v(33.4, 43.9) * mm, "end": v(33.4, 27.48) * mm});
            skLineSegment(sketch, "E162", {"start": v(33.4, 27.48) * mm, "end": v(31.4, 27.48) * mm});
            skLineSegment(sketch, "E163", {"start": v(48.16, 43.9) * mm, "end": v(48.16, 27.48) * mm});
            skLineSegment(sketch, "E164", {"start": v(48.16, 27.48) * mm, "end": v(50.85, 27.48) * mm});
            skLineSegment(sketch, "E165", {"start": v(50.85, 27.48) * mm, "end": v(50.85, 43.9) * mm});
            skLineSegment(sketch, "E166", {"start": v(50.85, 43.9) * mm, "end": v(48.16, 43.9) * mm});
            skLineSegment(sketch, "E167", {"start": v(63.38, 43.9) * mm, "end": v(63.38, 27.48) * mm});
            skLineSegment(sketch, "E168", {"start": v(63.38, 27.48) * mm, "end": v(65.3, 27.48) * mm});
            skLineSegment(sketch, "E169", {"start": v(65.3, 27.48) * mm, "end": v(65.3, 43.9) * mm});
            skLineSegment(sketch, "E170", {"start": v(65.3, 43.9) * mm, "end": v(63.38, 43.9) * mm});
            skLineSegment(sketch, "E171", {"start": v(79.06, 43.9) * mm, "end": v(79.06, 27.48) * mm});
            skLineSegment(sketch, "E172", {"start": v(79.06, 27.48) * mm, "end": v(81.45, 27.48) * mm});
            skLineSegment(sketch, "E173", {"start": v(81.45, 27.48) * mm, "end": v(81.45, 43.9) * mm});
            skLineSegment(sketch, "E174", {"start": v(81.45, 43.9) * mm, "end": v(79.06, 43.9) * mm});
            skLineSegment(sketch, "E175", {"start": v(93.97, 43.9) * mm, "end": v(93.97, 27.48) * mm});
            skLineSegment(sketch, "E176", {"start": v(93.97, 27.48) * mm, "end": v(96.82, 27.72) * mm});
            skLineSegment(sketch, "E177", {"start": v(96.82, 27.72) * mm, "end": v(96.82, 43.9) * mm});
            skLineSegment(sketch, "E178", {"start": v(96.82, 43.9) * mm, "end": v(93.97, 43.9) * mm});
            skLineSegment(sketch, "E179", {"start": v(108.42, 43.9) * mm, "end": v(108.42, 27.48) * mm});
            skLineSegment(sketch, "E180", {"start": v(108.42, 27.48) * mm, "end": v(111.27, 27.48) * mm});
            skLineSegment(sketch, "E181", {"start": v(111.27, 27.48) * mm, "end": v(111.27, 43.9) * mm});
            skLineSegment(sketch, "E182", {"start": v(111.27, 43.9) * mm, "end": v(108.42, 43.9) * mm});
            skLineSegment(sketch, "E183", {"start": v(-20.1, 43.9) * mm, "end": v(-22.68, 43.9) * mm});
            skLineSegment(sketch, "E184", {"start": v(-22.68, 43.9) * mm, "end": v(-22.68, 27.48) * mm});
            skLineSegment(sketch, "E185", {"start": v(-22.68, 27.48) * mm, "end": v(-19.78, 27.48) * mm});
            skLineSegment(sketch, "E186", {"start": v(-19.78, 27.48) * mm, "end": v(-20.1, 43.9) * mm});
            skLineSegment(sketch, "E187", {"start": v(-15.2, 23.12) * mm, "end": v(-15.2, 10.4) * mm});
            skLineSegment(sketch, "E188", {"start": v(-15.2, 10.4) * mm, "end": v(-12.55, 10.4) * mm});
            skLineSegment(sketch, "E189", {"start": v(-12.55, 10.4) * mm, "end": v(-12.55, 23.3) * mm});
            skLineSegment(sketch, "E190", {"start": v(-12.55, 23.3) * mm, "end": v(-15.2, 23.12) * mm});
            skLineSegment(sketch, "E191", {"start": v(-15.2, 23.12) * mm, "end": v(-12.55, 23.3) * mm});
            skLineSegment(sketch, "E192", {"start": v(2.65, 23.12) * mm, "end": v(2.65, 10.4) * mm});
            skLineSegment(sketch, "E193", {"start": v(2.65, 10.4) * mm, "end": v(5.5, 10.4) * mm});
            skLineSegment(sketch, "E194", {"start": v(5.5, 10.4) * mm, "end": v(5.5, 23.3) * mm});
            skLineSegment(sketch, "E195", {"start": v(5.5, 23.3) * mm, "end": v(2.65, 23.12) * mm});
            skLineSegment(sketch, "E196", {"start": v(2.65, 23.12) * mm, "end": v(5.5, 23.3) * mm});
            skLineSegment(sketch, "E197", {"start": v(21.27, 23.12) * mm, "end": v(21.27, 10.4) * mm});
            skLineSegment(sketch, "E198", {"start": v(21.27, 10.4) * mm, "end": v(24.31, 10.4) * mm});
            skLineSegment(sketch, "E199", {"start": v(24.31, 10.4) * mm, "end": v(24.31, 23.12) * mm});
            skLineSegment(sketch, "E200", {"start": v(24.31, 23.12) * mm, "end": v(21.27, 23.12) * mm});
            skLineSegment(sketch, "E201", {"start": v(38.56, 23.12) * mm, "end": v(38.56, 10.4) * mm});
            skLineSegment(sketch, "E202", {"start": v(38.56, 10.4) * mm, "end": v(41.6, 10.4) * mm});
            skLineSegment(sketch, "E203", {"start": v(41.6, 10.4) * mm, "end": v(41.6, 23.12) * mm});
            skLineSegment(sketch, "E204", {"start": v(41.6, 23.12) * mm, "end": v(38.56, 23.12) * mm});
            skLineSegment(sketch, "E205", {"start": v(55.47, 23.12) * mm, "end": v(55.47, 10.4) * mm});
            skLineSegment(sketch, "E206", {"start": v(55.47, 10.4) * mm, "end": v(58.32, 10.4) * mm});
            skLineSegment(sketch, "E207", {"start": v(58.32, 10.4) * mm, "end": v(58.32, 23.12) * mm});
            skLineSegment(sketch, "E208", {"start": v(58.32, 23.12) * mm, "end": v(55.47, 23.12) * mm});
            skLineSegment(sketch, "E209", {"start": v(69.72, 23.12) * mm, "end": v(69.72, 10.4) * mm});
            skLineSegment(sketch, "E210", {"start": v(69.72, 10.4) * mm, "end": v(72.2, 10.4) * mm});
            skLineSegment(sketch, "E211", {"start": v(72.2, 10.4) * mm, "end": v(72.2, 23.12) * mm});
            skLineSegment(sketch, "E212", {"start": v(72.2, 23.12) * mm, "end": v(69.72, 23.12) * mm});
            skLineSegment(sketch, "E213", {"start": v(86.25, 23.12) * mm, "end": v(86.25, 10.4) * mm});
            skLineSegment(sketch, "E214", {"start": v(86.25, 10.4) * mm, "end": v(88.34, 10.4) * mm});
            skLineSegment(sketch, "E215", {"start": v(88.34, 10.4) * mm, "end": v(88.34, 23.12) * mm});
            skLineSegment(sketch, "E216", {"start": v(88.34, 23.12) * mm, "end": v(86.25, 23.12) * mm});
            skLineSegment(sketch, "E217", {"start": v(101.64, 23.12) * mm, "end": v(101.64, 10.4) * mm});
            skLineSegment(sketch, "E218", {"start": v(101.64, 10.4) * mm, "end": v(104.68, 10.4) * mm});
            skLineSegment(sketch, "E219", {"start": v(104.68, 10.4) * mm, "end": v(104.68, 23.12) * mm});
            skLineSegment(sketch, "E220", {"start": v(104.68, 23.12) * mm, "end": v(101.64, 23.12) * mm});
            skLineSegment(sketch, "E221", {"start": v(-23.38, 6.4) * mm, "end": v(-23.1, -7.85) * mm});
            skLineSegment(sketch, "E222", {"start": v(-23.1, -7.85) * mm, "end": v(-20.33, -7.8) * mm});
            skLineSegment(sketch, "E223", {"start": v(-20.33, -7.8) * mm, "end": v(-20.6, 6.2) * mm});
            skLineSegment(sketch, "E224", {"start": v(-20.6, 6.2) * mm, "end": v(-23.38, 6.4) * mm});
            skLineSegment(sketch, "E225", {"start": v(-6.85, 6.4) * mm, "end": v(-6.58, -7.46) * mm});
            skLineSegment(sketch, "E226", {"start": v(-6.58, -7.46) * mm, "end": v(-3.03, -7.4) * mm});
            skLineSegment(sketch, "E227", {"start": v(-3.03, -7.4) * mm, "end": v(-3.3, 6.4) * mm});
            skLineSegment(sketch, "E228", {"start": v(-3.3, 6.4) * mm, "end": v(-6.85, 6.4) * mm});
            skLineSegment(sketch, "E229", {"start": v(11.58, 6.4) * mm, "end": v(11.85, -7.3) * mm});
            skLineSegment(sketch, "E230", {"start": v(11.85, -7.3) * mm, "end": v(15, -7.23) * mm});
            skLineSegment(sketch, "E231", {"start": v(15, -7.23) * mm, "end": v(14.73, 6.4) * mm});
            skLineSegment(sketch, "E232", {"start": v(14.73, 6.4) * mm, "end": v(11.58, 6.4) * mm});
            skLineSegment(sketch, "E233", {"start": v(29.82, 6.4) * mm, "end": v(30.09, -7.3) * mm});
            skLineSegment(sketch, "E234", {"start": v(30.09, -7.3) * mm, "end": v(32.86, -7.24) * mm});
            skLineSegment(sketch, "E235", {"start": v(32.86, -7.24) * mm, "end": v(32.6, 6.4) * mm});
            skLineSegment(sketch, "E236", {"start": v(32.6, 6.4) * mm, "end": v(29.82, 6.4) * mm});
            skLineSegment(sketch, "E237", {"start": v(47.3, 6.4) * mm, "end": v(47.57, -7.3) * mm});
            skLineSegment(sketch, "E238", {"start": v(47.57, -7.3) * mm, "end": v(49.77, -7.28) * mm});
            skLineSegment(sketch, "E239", {"start": v(49.77, -7.28) * mm, "end": v(49.5, 6.4) * mm});
            skLineSegment(sketch, "E240", {"start": v(49.5, 6.4) * mm, "end": v(47.3, 6.4) * mm});
            skLineSegment(sketch, "E241", {"start": v(62.88, 6.4) * mm, "end": v(63.15, -7.3) * mm});
            skLineSegment(sketch, "E242", {"start": v(63.15, -7.3) * mm, "end": v(65.74, -7.24) * mm});
            skLineSegment(sketch, "E243", {"start": v(65.74, -7.24) * mm, "end": v(65.47, 6.4) * mm});
            skLineSegment(sketch, "E244", {"start": v(65.47, 6.4) * mm, "end": v(62.88, 6.4) * mm});
            skLineSegment(sketch, "E245", {"start": v(78.08, 6.4) * mm, "end": v(78.35, -7.3) * mm});
            skLineSegment(sketch, "E246", {"start": v(78.35, -7.3) * mm, "end": v(81.13, -7.24) * mm});
            skLineSegment(sketch, "E247", {"start": v(81.13, -7.24) * mm, "end": v(80.86, 6.4) * mm});
            skLineSegment(sketch, "E248", {"start": v(80.86, 6.4) * mm, "end": v(78.08, 6.4) * mm});
            skLineSegment(sketch, "E249", {"start": v(93.66, 6.4) * mm, "end": v(93.93, -7.3) * mm});
            skLineSegment(sketch, "E250", {"start": v(93.93, -7.3) * mm, "end": v(96.51, -7.24) * mm});
            skLineSegment(sketch, "E251", {"start": v(96.51, -7.24) * mm, "end": v(96.24, 6.4) * mm});
            skLineSegment(sketch, "E252", {"start": v(96.24, 6.4) * mm, "end": v(93.66, 6.4) * mm});
            skLineSegment(sketch, "E253", {"start": v(109.24, 6.4) * mm, "end": v(109.5, -7.3) * mm});
            skLineSegment(sketch, "E254", {"start": v(109.5, -7.3) * mm, "end": v(112.28, -7.24) * mm});
            skLineSegment(sketch, "E255", {"start": v(112.28, -7.24) * mm, "end": v(112.01, 6.4) * mm});
            skLineSegment(sketch, "E256", {"start": v(112.01, 6.4) * mm, "end": v(109.24, 6.6) * mm});
            skLineSegment(sketch, "E257", {"start": v(109.24, 6.6) * mm, "end": v(112.01, 6.4) * mm});
            skSolve(sketch);
        }
        {
            var Q0;
            Q0 = qSketchRegion(id + "F35", true);
            extrude(context, id + "F36", {"entities" : qUnion([Q0]), "operationType" : NewBodyOperationType.ADD, "depth" : 1.78 * mm, "offsetDistance" : 25.4 * mm});
        }
        {
            var Q0;
            {var subQ0=sQuery(id+"F4.wireOp",EDGE,"E16.MirrorCS");Q0=makeQuery(id+"F18.boolean.opBoolean","MERGE",FACE,{"derivedFrom":[makeQuery(id+"F6.boolean.opBoolean","MERGE",FACE,{"derivedFrom":[makeQuery(id+"F5.opExtrude","SWEPT_FACE",FACE,{"disambiguationData":[OSD([subQ0])]}),makeQuery(id+"F6.opExtrude","SWEPT_FACE",FACE,{"disambiguationData":[OSD([subQ0])]})]}),makeQuery(id+"F18.opExtrude","SWEPT_FACE",FACE,{"disambiguationData":[OSD([sQuery(id+"F17.wireOp",EDGE,"E51")])]})]});}
            var sketch = newSketch(context, id + "F37", { "sketchPlane" : qUnion([Q0])});
            skLineSegment(sketch, "E258", {"start": v(-115.57, 45.45) * mm, "end": v(-57.05, 45.45) * mm});
            skLineSegment(sketch, "E259", {"start": v(-57.05, 45.45) * mm, "end": v(-58.09, 44.22) * mm});
            skLineSegment(sketch, "E260", {"start": v(-115.57, 45.45) * mm, "end": v(-115.57, 42.91) * mm});
            skLineSegment(sketch, "E261", {"start": v(-115.57, 42.91) * mm, "end": v(-59.19, 42.91) * mm});
            skLineSegment(sketch, "E262", {"start": v(-59.19, 42.91) * mm, "end": v(-57.05, 45.45) * mm});
            skLineSegment(sketch, "E263", {"start": v(-41.86, 45.45) * mm, "end": v(25.9, 45.45) * mm});
            skLineSegment(sketch, "E264", {"start": v(25.9, 45.45) * mm, "end": v(25.9, 42.27) * mm});
            skLineSegment(sketch, "E265", {"start": v(25.9, 42.27) * mm, "end": v(-38.97, 42.27) * mm});
            skLineSegment(sketch, "E266", {"start": v(-38.97, 42.27) * mm, "end": v(-41.86, 45.45) * mm});
            skLineSegment(sketch, "E267", {"start": v(-115.57, 27.47) * mm, "end": v(-64.2, 27.47) * mm});
            skLineSegment(sketch, "E268", {"start": v(-64.2, 27.47) * mm, "end": v(-64.2, 23.13) * mm});
            skLineSegment(sketch, "E269", {"start": v(-64.2, 23.13) * mm, "end": v(-115.57, 23.13) * mm});
            skLineSegment(sketch, "E270", {"start": v(-115.57, 23.13) * mm, "end": v(-115.57, 27.47) * mm});
            skLineSegment(sketch, "E271", {"start": v(-35.25, 27.47) * mm, "end": v(25.9, 27.47) * mm});
            skLineSegment(sketch, "E272", {"start": v(25.9, 27.47) * mm, "end": v(25.9, 23.18) * mm});
            skLineSegment(sketch, "E273", {"start": v(25.9, 23.18) * mm, "end": v(-35.25, 23.18) * mm});
            skLineSegment(sketch, "E274", {"start": v(-35.25, 23.18) * mm, "end": v(-35.25, 27.47) * mm});
            skLineSegment(sketch, "E275", {"start": v(-115.57, 9.54) * mm, "end": v(25.9, 9.54) * mm});
            skLineSegment(sketch, "E276", {"start": v(25.9, 9.54) * mm, "end": v(25.9, 5.96) * mm});
            skLineSegment(sketch, "E277", {"start": v(25.9, 5.96) * mm, "end": v(-115.57, 5.96) * mm});
            skLineSegment(sketch, "E278", {"start": v(-115.57, 5.96) * mm, "end": v(-115.57, 9.54) * mm});
            skSolve(sketch);
        }
        {
            var Q0;
            Q0 = qSketchRegion(id + "F37", true);
            extrude(context, id + "F38", {"entities" : qUnion([Q0]), "operationType" : NewBodyOperationType.ADD, "depth" : 3.05 * mm, "offsetDistance" : 25.4 * mm});
        }
        {
            var Q0;
            {var subQ0=sQuery(id+"F4.wireOp",EDGE,"E14");var subQ2=sQuery(id+"F4.wireOp",EDGE,"E16.MirrorCS");var subQ3=sQuery(id+"F17.wireOp",EDGE,"E51");Q0=makeQuery(id+"F38.boolean.opBoolean","SPLIT",FACE,{"disambiguationData":[TD([makeQuery(id+"F5.opExtrude","SWEPT_FACE",FACE,{"disambiguationData":[OSD([subQ0])]})])],"derivedFrom":makeQuery(id+"F18.boolean.opBoolean","MERGE",FACE,{"derivedFrom":[makeQuery(id+"F6.boolean.opBoolean","MERGE",FACE,{"derivedFrom":[makeQuery(id+"F5.opExtrude","SWEPT_FACE",FACE,{"disambiguationData":[OSD([subQ2])]}),makeQuery(id+"F6.opExtrude","SWEPT_FACE",FACE,{"disambiguationData":[OSD([subQ2])]})]}),makeQuery(id+"F18.opExtrude","SWEPT_FACE",FACE,{"disambiguationData":[OSD([subQ3])]})]})});}
            var sketch = newSketch(context, id + "F39", { "sketchPlane" : qUnion([Q0])});
            skLineSegment(sketch, "E279", {"start": v(-101.36, 62.54) * mm, "end": v(-101.36, 45.45) * mm});
            skLineSegment(sketch, "E280", {"start": v(-101.36, 45.45) * mm, "end": v(-99.13, 45.45) * mm});
            skLineSegment(sketch, "E281", {"start": v(-99.13, 45.45) * mm, "end": v(-99.13, 62.54) * mm});
            skLineSegment(sketch, "E282", {"start": v(-99.13, 62.54) * mm, "end": v(-101.36, 62.54) * mm});
            skLineSegment(sketch, "E283", {"start": v(-88, 62.54) * mm, "end": v(-85.9, 62.54) * mm});
            skLineSegment(sketch, "E284", {"start": v(-85.9, 62.54) * mm, "end": v(-85.9, 45.45) * mm});
            skLineSegment(sketch, "E285", {"start": v(-85.9, 45.45) * mm, "end": v(-88, 45.45) * mm});
            skLineSegment(sketch, "E286", {"start": v(-88, 45.45) * mm, "end": v(-88, 62.54) * mm});
            skLineSegment(sketch, "E287", {"start": v(-74.54, 62.54) * mm, "end": v(-72.18, 62.54) * mm});
            skLineSegment(sketch, "E288", {"start": v(-72.18, 62.54) * mm, "end": v(-72.18, 45.45) * mm});
            skLineSegment(sketch, "E289", {"start": v(-72.18, 45.45) * mm, "end": v(-74.54, 45.45) * mm});
            skLineSegment(sketch, "E290", {"start": v(-74.54, 45.45) * mm, "end": v(-74.54, 62.54) * mm});
            skLineSegment(sketch, "E291", {"start": v(-58.27, 62.54) * mm, "end": v(-56.7, 62.54) * mm});
            skLineSegment(sketch, "E292", {"start": v(-56.7, 62.54) * mm, "end": v(-56.7, 45.86) * mm});
            skLineSegment(sketch, "E293", {"start": v(-56.7, 45.86) * mm, "end": v(-57.05, 45.45) * mm});
            skLineSegment(sketch, "E294", {"start": v(-57.05, 45.45) * mm, "end": v(-58.27, 45.45) * mm});
            skLineSegment(sketch, "E295", {"start": v(-58.27, 45.45) * mm, "end": v(-58.27, 62.54) * mm});
            skLineSegment(sketch, "E296", {"start": v(-42.62, 62.54) * mm, "end": v(-40.84, 62.54) * mm});
            skLineSegment(sketch, "E297", {"start": v(-40.84, 62.54) * mm, "end": v(-40.84, 45.86) * mm});
            skLineSegment(sketch, "E298", {"start": v(-42.62, 62.54) * mm, "end": v(-42.62, 46.29) * mm});
            skLineSegment(sketch, "E299", {"start": v(-42.62, 46.29) * mm, "end": v(-41.86, 45.45) * mm});
            skLineSegment(sketch, "E300", {"start": v(-41.86, 45.45) * mm, "end": v(-40.84, 45.45) * mm});
            skLineSegment(sketch, "E301", {"start": v(-40.84, 45.45) * mm, "end": v(-40.84, 45.86) * mm});
            skLineSegment(sketch, "E302", {"start": v(-25.37, 62.54) * mm, "end": v(-23.42, 62.54) * mm});
            skLineSegment(sketch, "E303", {"start": v(-23.42, 62.54) * mm, "end": v(-23.42, 45.45) * mm});
            skLineSegment(sketch, "E304", {"start": v(-23.42, 45.45) * mm, "end": v(-25.37, 45.45) * mm});
            skLineSegment(sketch, "E305", {"start": v(-25.37, 45.45) * mm, "end": v(-25.37, 62.54) * mm});
            skLineSegment(sketch, "E306", {"start": v(-7.35, 62.54) * mm, "end": v(-5.79, 62.54) * mm});
            skLineSegment(sketch, "E307", {"start": v(-5.79, 62.54) * mm, "end": v(-5.79, 45.86) * mm});
            skLineSegment(sketch, "E308", {"start": v(-5.79, 45.86) * mm, "end": v(-5.79, 45.45) * mm});
            skLineSegment(sketch, "E309", {"start": v(-5.79, 45.45) * mm, "end": v(-7.35, 45.45) * mm});
            skLineSegment(sketch, "E310", {"start": v(-7.35, 45.45) * mm, "end": v(-7.35, 62.54) * mm});
            skLineSegment(sketch, "E311", {"start": v(12.63, 62.54) * mm, "end": v(14.2, 62.54) * mm});
            skLineSegment(sketch, "E312", {"start": v(14.2, 62.54) * mm, "end": v(14.2, 45.86) * mm});
            skLineSegment(sketch, "E313", {"start": v(12.63, 45.45) * mm, "end": v(12.63, 62.54) * mm});
            skLineSegment(sketch, "E314", {"start": v(12.63, 45.45) * mm, "end": v(14.2, 45.45) * mm});
            skLineSegment(sketch, "E315", {"start": v(14.2, 45.45) * mm, "end": v(14.2, 45.86) * mm});
            skLineSegment(sketch, "E316", {"start": v(-111.5, 42.86) * mm, "end": v(-111.5, 27.49) * mm});
            skLineSegment(sketch, "E317", {"start": v(-111.5, 27.49) * mm, "end": v(-109.18, 27.49) * mm});
            skLineSegment(sketch, "E318", {"start": v(-109.18, 27.49) * mm, "end": v(-109.18, 42.97) * mm});
            skLineSegment(sketch, "E319", {"start": v(-109.18, 42.97) * mm, "end": v(-111.5, 42.86) * mm});
            skLineSegment(sketch, "E320", {"start": v(-95.9, 42.86) * mm, "end": v(-95.9, 27.37) * mm});
            skLineSegment(sketch, "E321", {"start": v(-95.9, 27.37) * mm, "end": v(-93.11, 27.37) * mm});
            skLineSegment(sketch, "E322", {"start": v(-93.11, 27.37) * mm, "end": v(-93.11, 42.86) * mm});
            skLineSegment(sketch, "E323", {"start": v(-93.11, 42.86) * mm, "end": v(-95.9, 42.86) * mm});
            skLineSegment(sketch, "E324", {"start": v(-81.82, 42.86) * mm, "end": v(-81.82, 27.49) * mm});
            skLineSegment(sketch, "E325", {"start": v(-81.82, 27.49) * mm, "end": v(-78.9, 27.49) * mm});
            skLineSegment(sketch, "E326", {"start": v(-78.9, 27.49) * mm, "end": v(-78.9, 42.86) * mm});
            skLineSegment(sketch, "E327", {"start": v(-78.9, 42.86) * mm, "end": v(-81.82, 42.86) * mm});
            skLineSegment(sketch, "E328", {"start": v(-67.27, 42.86) * mm, "end": v(-67.27, 27.72) * mm});
            skLineSegment(sketch, "E329", {"start": v(-67.27, 27.72) * mm, "end": v(-65.17, 27.72) * mm});
            skLineSegment(sketch, "E330", {"start": v(-65.17, 27.72) * mm, "end": v(-65.17, 34.29) * mm});
            skLineSegment(sketch, "E331", {"start": v(-65.17, 34.29) * mm, "end": v(-66.42, 34.29) * mm});
            skLineSegment(sketch, "E332", {"start": v(-66.42, 34.29) * mm, "end": v(-65.17, 36.2) * mm});
            skLineSegment(sketch, "E333", {"start": v(-65.17, 36.2) * mm, "end": v(-65.17, 42.86) * mm});
            skLineSegment(sketch, "E334", {"start": v(-65.17, 42.86) * mm, "end": v(-67.27, 42.86) * mm});
            skLineSegment(sketch, "E335", {"start": v(-32.4, 42.86) * mm, "end": v(-32.4, 27.33) * mm});
            skLineSegment(sketch, "E336", {"start": v(-32.4, 27.33) * mm, "end": v(-30.36, 27.33) * mm});
            skLineSegment(sketch, "E337", {"start": v(-30.36, 27.33) * mm, "end": v(-30.36, 42.86) * mm});
            skLineSegment(sketch, "E338", {"start": v(-30.36, 42.86) * mm, "end": v(-30.36, 42.3) * mm});
            skLineSegment(sketch, "E339", {"start": v(-30.36, 42.3) * mm, "end": v(-32.4, 42.3) * mm});
            skLineSegment(sketch, "E340", {"start": v(-32.4, 42.3) * mm, "end": v(-30.36, 42.3) * mm});
            skLineSegment(sketch, "E341", {"start": v(-18.35, 42.22) * mm, "end": v(-18.35, 27.47) * mm});
            skLineSegment(sketch, "E342", {"start": v(-18.35, 27.47) * mm, "end": v(-16.05, 27.47) * mm});
            skLineSegment(sketch, "E343", {"start": v(-16.05, 27.47) * mm, "end": v(-16.05, 42.3) * mm});
            skLineSegment(sketch, "E344", {"start": v(-16.05, 42.3) * mm, "end": v(-18.35, 42.22) * mm});
            skLineSegment(sketch, "E345", {"start": v(0.74, 42.22) * mm, "end": v(0.74, 27.53) * mm});
            skLineSegment(sketch, "E346", {"start": v(0.74, 27.53) * mm, "end": v(2.57, 27.53) * mm});
            skLineSegment(sketch, "E347", {"start": v(2.57, 27.53) * mm, "end": v(2.57, 42.22) * mm});
            skLineSegment(sketch, "E348", {"start": v(2.57, 42.22) * mm, "end": v(0.74, 42.22) * mm});
            skLineSegment(sketch, "E349", {"start": v(18.45, 42.22) * mm, "end": v(18.45, 27.5) * mm});
            skLineSegment(sketch, "E350", {"start": v(18.45, 27.5) * mm, "end": v(20.18, 27.5) * mm});
            skLineSegment(sketch, "E351", {"start": v(20.18, 27.5) * mm, "end": v(20.18, 42.22) * mm});
            skLineSegment(sketch, "E352", {"start": v(20.18, 42.22) * mm, "end": v(18.45, 42.22) * mm});
            skLineSegment(sketch, "E353", {"start": v(-104.23, 23.5) * mm, "end": v(-104.23, 9.9) * mm});
            skLineSegment(sketch, "E354", {"start": v(-104.23, 9.9) * mm, "end": v(-102.05, 9.9) * mm});
            skLineSegment(sketch, "E355", {"start": v(-102.05, 9.9) * mm, "end": v(-102.05, 23.5) * mm});
            skLineSegment(sketch, "E356", {"start": v(-102.05, 23.5) * mm, "end": v(-104.23, 23.5) * mm});
            skLineSegment(sketch, "E357", {"start": v(-88.57, 23.5) * mm, "end": v(-88.57, 9.8) * mm});
            skLineSegment(sketch, "E358", {"start": v(-88.57, 9.8) * mm, "end": v(-86.6, 9.8) * mm});
            skLineSegment(sketch, "E359", {"start": v(-86.6, 9.8) * mm, "end": v(-86.6, 23.5) * mm});
            skLineSegment(sketch, "E360", {"start": v(-86.6, 23.5) * mm, "end": v(-88.57, 23.5) * mm});
            skLineSegment(sketch, "E361", {"start": v(-74.75, 23.5) * mm, "end": v(-74.75, 9.97) * mm});
            skLineSegment(sketch, "E362", {"start": v(-74.75, 9.97) * mm, "end": v(-72.43, 9.97) * mm});
            skLineSegment(sketch, "E363", {"start": v(-72.43, 9.97) * mm, "end": v(-72.43, 23.5) * mm});
            skLineSegment(sketch, "E364", {"start": v(-72.43, 23.5) * mm, "end": v(-74.75, 23.5) * mm});
            skLineSegment(sketch, "E365", {"start": v(-26.11, 23.5) * mm, "end": v(-26.11, 10.24) * mm});
            skLineSegment(sketch, "E366", {"start": v(-26.11, 10.24) * mm, "end": v(-23.95, 10.18) * mm});
            skLineSegment(sketch, "E367", {"start": v(-23.95, 10.18) * mm, "end": v(-23.95, 23.5) * mm});
            skLineSegment(sketch, "E368", {"start": v(-23.95, 23.5) * mm, "end": v(-26.11, 23.5) * mm});
            skLineSegment(sketch, "E369", {"start": v(-9.98, 23.5) * mm, "end": v(-9.98, 10.24) * mm});
            skLineSegment(sketch, "E370", {"start": v(-9.98, 10.24) * mm, "end": v(-7.69, 10.24) * mm});
            skLineSegment(sketch, "E371", {"start": v(-7.69, 10.24) * mm, "end": v(-7.69, 23.5) * mm});
            skLineSegment(sketch, "E372", {"start": v(-7.69, 23.5) * mm, "end": v(-9.98, 23.5) * mm});
            skLineSegment(sketch, "E373", {"start": v(8.58, 10.24) * mm, "end": v(8.58, 23.5) * mm});
            skLineSegment(sketch, "E374", {"start": v(8.58, 23.5) * mm, "end": v(11.34, 23.5) * mm});
            skLineSegment(sketch, "E375", {"start": v(11.34, 23.5) * mm, "end": v(11.34, 10.24) * mm});
            skLineSegment(sketch, "E376", {"start": v(11.34, 10.24) * mm, "end": v(8.58, 10.24) * mm});
            skLineSegment(sketch, "E377", {"start": v(17.5, 6.5) * mm, "end": v(17.5, -7.44) * mm});
            skLineSegment(sketch, "E378", {"start": v(17.5, -7.44) * mm, "end": v(20.6, -7.44) * mm});
            skLineSegment(sketch, "E379", {"start": v(20.6, -7.44) * mm, "end": v(20.6, 6.44) * mm});
            skLineSegment(sketch, "E380", {"start": v(20.6, 6.44) * mm, "end": v(17.5, 6.5) * mm});
            skLineSegment(sketch, "E381", {"start": v(2.61, 6.5) * mm, "end": v(2.61, -7.52) * mm});
            skLineSegment(sketch, "E382", {"start": v(2.61, -7.52) * mm, "end": v(0, -7.52) * mm});
            skLineSegment(sketch, "E383", {"start": v(0, -7.52) * mm, "end": v(0, 6.5) * mm});
            skLineSegment(sketch, "E384", {"start": v(0, 6.5) * mm, "end": v(2.61, 6.5) * mm});
            skLineSegment(sketch, "E385", {"start": v(-15.27, 6.5) * mm, "end": v(-15.27, -7.94) * mm});
            skLineSegment(sketch, "E386", {"start": v(-15.27, -7.94) * mm, "end": v(-17.72, -7.94) * mm});
            skLineSegment(sketch, "E387", {"start": v(-17.72, -7.94) * mm, "end": v(-17.72, 6.5) * mm});
            skLineSegment(sketch, "E388", {"start": v(-17.72, 6.5) * mm, "end": v(-15.27, 6.5) * mm});
            skLineSegment(sketch, "E389", {"start": v(-31.87, 6.5) * mm, "end": v(-31.87, -7.53) * mm});
            skLineSegment(sketch, "E390", {"start": v(-31.87, -7.53) * mm, "end": v(-34.37, -7.53) * mm});
            skLineSegment(sketch, "E391", {"start": v(-34.37, -7.53) * mm, "end": v(-34.37, 6.5) * mm});
            skLineSegment(sketch, "E392", {"start": v(-34.37, 6.5) * mm, "end": v(-31.87, 6.5) * mm});
            skLineSegment(sketch, "E393", {"start": v(-82.15, 6.5) * mm, "end": v(-82.15, -7.48) * mm});
            skLineSegment(sketch, "E394", {"start": v(-82.15, -7.48) * mm, "end": v(-79.85, -7.48) * mm});
            skLineSegment(sketch, "E395", {"start": v(-79.85, -7.48) * mm, "end": v(-79.85, 6.5) * mm});
            skLineSegment(sketch, "E396", {"start": v(-79.85, 6.5) * mm, "end": v(-82.15, 6.5) * mm});
            skLineSegment(sketch, "E397", {"start": v(-67.28, 6.5) * mm, "end": v(-67.28, -7.75) * mm});
            skLineSegment(sketch, "E398", {"start": v(-67.28, -7.75) * mm, "end": v(-64.5, -7.75) * mm});
            skLineSegment(sketch, "E399", {"start": v(-64.5, -7.75) * mm, "end": v(-64.5, 6.5) * mm});
            skLineSegment(sketch, "E400", {"start": v(-64.5, 6.5) * mm, "end": v(-67.28, 6.5) * mm});
            skLineSegment(sketch, "E401", {"start": v(-52.6, 6.5) * mm, "end": v(-52.6, -7.58) * mm});
            skLineSegment(sketch, "E402", {"start": v(-52.6, -7.58) * mm, "end": v(-50.18, -7.58) * mm});
            skLineSegment(sketch, "E403", {"start": v(-50.18, -7.58) * mm, "end": v(-50.18, 6.5) * mm});
            skLineSegment(sketch, "E404", {"start": v(-50.18, 6.5) * mm, "end": v(-52.6, 6.5) * mm});
            skPoint(sketch, "E405.end.orphan", {"position": v(-53.47, 10.24) * mm});
            skLineSegment(sketch, "E406", {"start": v(-60.73, 12.23) * mm, "end": v(-60.73, 10.13) * mm});
            skLineSegment(sketch, "E407", {"start": v(-60.73, 10.13) * mm, "end": v(-59, 10) * mm});
            skLineSegment(sketch, "E408", {"start": v(-59, 10) * mm, "end": v(-59, 12.06) * mm});
            skLineSegment(sketch, "E409", {"start": v(-59, 12.06) * mm, "end": v(-60.73, 12.23) * mm});
            skLineSegment(sketch, "E410", {"start": v(-45.25, 12.23) * mm, "end": v(-45.25, 10.13) * mm});
            skLineSegment(sketch, "E411", {"start": v(-45.25, 10.13) * mm, "end": v(-43.51, 10) * mm});
            skLineSegment(sketch, "E412", {"start": v(-43.51, 10) * mm, "end": v(-43.51, 12.23) * mm});
            skLineSegment(sketch, "E413", {"start": v(-43.51, 12.23) * mm, "end": v(-45.25, 12.23) * mm});
            skLineSegment(sketch, "E414", {"start": v(-97.93, 6.54) * mm, "end": v(-97.93, -7.29) * mm});
            skLineSegment(sketch, "E415", {"start": v(-97.93, -7.29) * mm, "end": v(-95.6, -7.29) * mm});
            skLineSegment(sketch, "E416", {"start": v(-95.6, -7.29) * mm, "end": v(-95.6, 6.13) * mm});
            skLineSegment(sketch, "E417", {"start": v(-95.6, 6.13) * mm, "end": v(-97.93, 6.54) * mm});
            skLineSegment(sketch, "E418", {"start": v(-112.5, 6.54) * mm, "end": v(-112.5, -7.44) * mm});
            skLineSegment(sketch, "E419", {"start": v(-112.5, -7.44) * mm, "end": v(-110.06, -7.44) * mm});
            skLineSegment(sketch, "E420", {"start": v(-110.06, -7.44) * mm, "end": v(-110.06, 6.54) * mm});
            skLineSegment(sketch, "E421", {"start": v(-110.06, 6.54) * mm, "end": v(-112.5, 6.54) * mm});
            skLineSegment(sketch, "E422", {"start": v(-112.5, 6.54) * mm, "end": v(-110.06, 6.54) * mm});
            skSolve(sketch);
        }
        {
            var Q0;
            Q0 = qSketchRegion(id + "F39", true);
            extrude(context, id + "F40", {"entities" : qUnion([Q0]), "operationType" : NewBodyOperationType.ADD, "depth" : 1.52 * mm, "offsetDistance" : 25.4 * mm});
        }
    });
